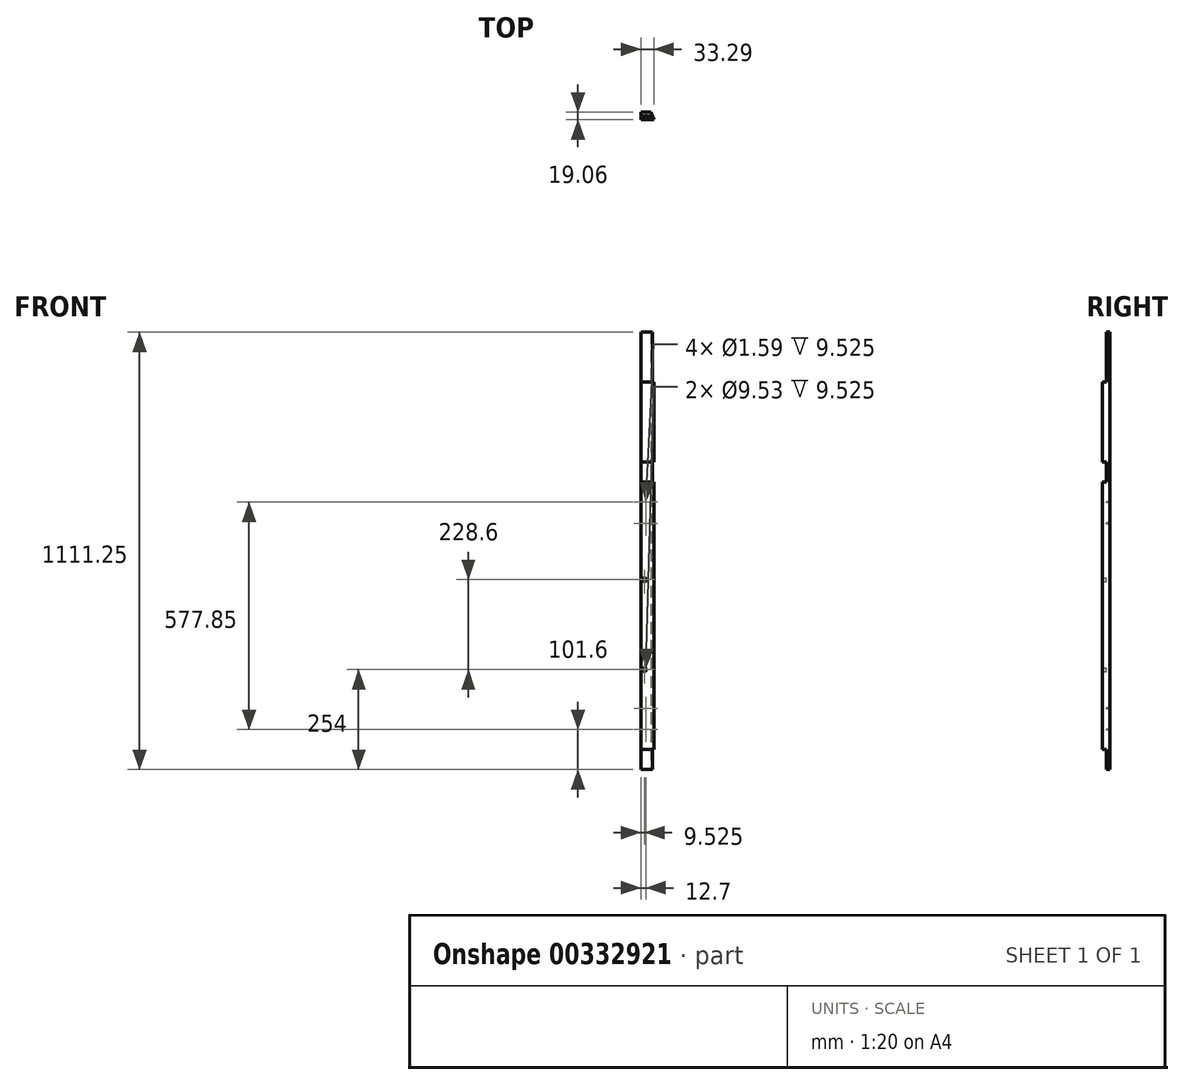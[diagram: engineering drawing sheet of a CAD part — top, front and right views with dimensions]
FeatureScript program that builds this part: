
annotation { "Feature Type Name" : "Feature", "Feature Type Description" : "" }
export const myFeature = defineFeature(function(context is Context, id is Id, definition is map)
    precondition{}
    {
        {
            var Q0;
            Q0=qCreatedBy(makeId("Top.planeOp"),FACE);
            var sketch = newSketch(context, id + "F0", { "sketchPlane" : qUnion([Q0])});
            skLineSegment(sketch, "E0.bottom", {"start": v(0, 9.53) * mm, "end": v(-25.4, 9.53) * mm});
            skLineSegment(sketch, "E0.top", {"start": v(7.9, -9.53) * mm, "end": v(-25.4, -9.53) * mm});
            skLineSegment(sketch, "E0.right", {"start": v(-25.4, 9.53) * mm, "end": v(-25.4, -9.53) * mm});
            skPoint(sketch, "E0.middle", {"position": v(0, 0) * mm});
            skLineSegment(sketch, "E1", {"start": v(0, 9.53) * mm, "end": v(7.9, -9.53) * mm});
            skPoint(sketch, "E0.left.end.orphan", {"position": v(25.4, -9.52) * mm});
            skPoint(sketch, "E2.orphan", {"position": v(25.4, 9.53) * mm});
            skSolve(sketch);
        }
        {
            var Q0;
            Q0=makeQuery(id+"F0.imprint","IMPRINT",FACE,{"disambiguationData":[TD([[makeQuery(id+"F0.imprint","IMPRINT",EDGE,{"derivedFrom":sQuery(id+"F0.wireOp",EDGE,"E0.bottom")}),1.0]])]});
            extrude(context, id + "F1", {"entities" : qUnion([Q0]), "depth" : 1111.25 * mm});
        }
        {
            var Q0;
            Q0=qCreatedBy(makeId("Front.planeOp"),FACE);
            var sketch = newSketch(context, id + "F2", { "sketchPlane" : qUnion([Q0])});
            skLineSegment(sketch, "E3.bottom", {"start": v(-38.77, 0) * mm, "end": v(83.66, 0) * mm});
            skLineSegment(sketch, "E3.top", {"start": v(-38.77, 50.8) * mm, "end": v(83.66, 50.8) * mm});
            skLineSegment(sketch, "E3.left", {"start": v(-38.77, 0) * mm, "end": v(-38.77, 50.8) * mm});
            skLineSegment(sketch, "E3.right", {"start": v(83.66, 0) * mm, "end": v(83.66, 50.8) * mm});
            skLineSegment(sketch, "E4.bottom", {"start": v(-44.21, 730.25) * mm, "end": v(49.65, 730.25) * mm});
            skLineSegment(sketch, "E4.top", {"start": v(-44.21, 781.05) * mm, "end": v(49.65, 781.05) * mm});
            skLineSegment(sketch, "E4.left", {"start": v(-44.21, 730.25) * mm, "end": v(-44.21, 781.05) * mm});
            skLineSegment(sketch, "E4.right", {"start": v(49.65, 730.25) * mm, "end": v(49.65, 781.05) * mm});
            skLineSegment(sketch, "E5.bottom", {"start": v(-210.36, 984.25) * mm, "end": v(132.8, 984.25) * mm});
            skLineSegment(sketch, "E5.top", {"start": v(-210.36, 1111.25) * mm, "end": v(132.8, 1111.25) * mm});
            skLineSegment(sketch, "E5.left", {"start": v(-210.36, 984.25) * mm, "end": v(-210.36, 1111.25) * mm});
            skLineSegment(sketch, "E5.right", {"start": v(132.8, 984.25) * mm, "end": v(132.8, 1111.25) * mm});
            skSolve(sketch);
        }
        {
            var Q0;
            Q0=qSketchRegion(id+"F2",true);
            extrude(context, id + "F3", {"entities" : qUnion([Q0]), "operationType" : NewBodyOperationType.REMOVE, "depth" : 25.4 * mm});
        }
        {
            var Q0;
            Q0=qCreatedBy(makeId("Front.planeOp"),FACE);
            var sketch = newSketch(context, id + "F4", { "sketchPlane" : qUnion([Q0])});
            skCircle(sketch, "E6", {"center": v(12.7, 101.6) * mm, "radius": 0.8 * mm});
            skCircle(sketch, "E7", {"center": v(12.7, 155.58) * mm, "radius": 0.8 * mm});
            skCircle(sketch, "E8", {"center": v(12.7, 625.48) * mm, "radius": 0.8 * mm});
            skCircle(sketch, "E9", {"center": v(12.7, 679.45) * mm, "radius": 0.8 * mm});
            skLineSegment(sketch, "E10", {"start": v(0, 0) * mm, "end": v(0, 1192.46) * mm, "construction": true});
            skLineSegment(sketch, "E11.bottom", {"start": v(12.7, 101.6) * mm, "end": v(-12.7, 101.6) * mm, "construction": true});
            skLineSegment(sketch, "E11.top", {"start": v(12.7, 679.45) * mm, "end": v(-12.7, 679.45) * mm, "construction": true});
            skLineSegment(sketch, "E11.left", {"start": v(12.7, 101.6) * mm, "end": v(12.7, 679.45) * mm, "construction": true});
            skLineSegment(sketch, "E11.right", {"start": v(-12.7, 101.6) * mm, "end": v(-12.7, 679.45) * mm, "construction": true});
            skCircle(sketch, "E12", {"center": v(-12.7, 625.48) * mm, "radius": 0.8 * mm});
            skCircle(sketch, "E13", {"center": v(-12.7, 679.45) * mm, "radius": 0.8 * mm});
            skCircle(sketch, "E14", {"center": v(-12.7, 101.6) * mm, "radius": 0.8 * mm});
            skCircle(sketch, "E15", {"center": v(-12.7, 155.58) * mm, "radius": 0.8 * mm});
            skSolve(sketch);
        }
        {
            var Q0;
            Q0=qSketchRegion(id+"F4",true);
            extrude(context, id + "F5", {"entities" : qUnion([Q0]), "operationType" : NewBodyOperationType.REMOVE, "oppositeDirection" : true, "depth" : 25.4 * mm});
        }
        {
            var Q0;
            Q0=qCreatedBy(makeId("Front.planeOp"),FACE);
            var sketch = newSketch(context, id + "F6", { "sketchPlane" : qUnion([Q0])});
            skCircle(sketch, "E16", {"center": v(-15.88, 254) * mm, "radius": 4.76 * mm});
            skCircle(sketch, "E17", {"center": v(-15.88, 482.6) * mm, "radius": 4.76 * mm});
            skSolve(sketch);
        }
        {
            var Q0;
            Q0=qSketchRegion(id+"F6",true);
            extrude(context, id + "F7", {"entities" : qUnion([Q0]), "operationType" : NewBodyOperationType.REMOVE, "depth" : 25.4 * mm});
        }
    });
